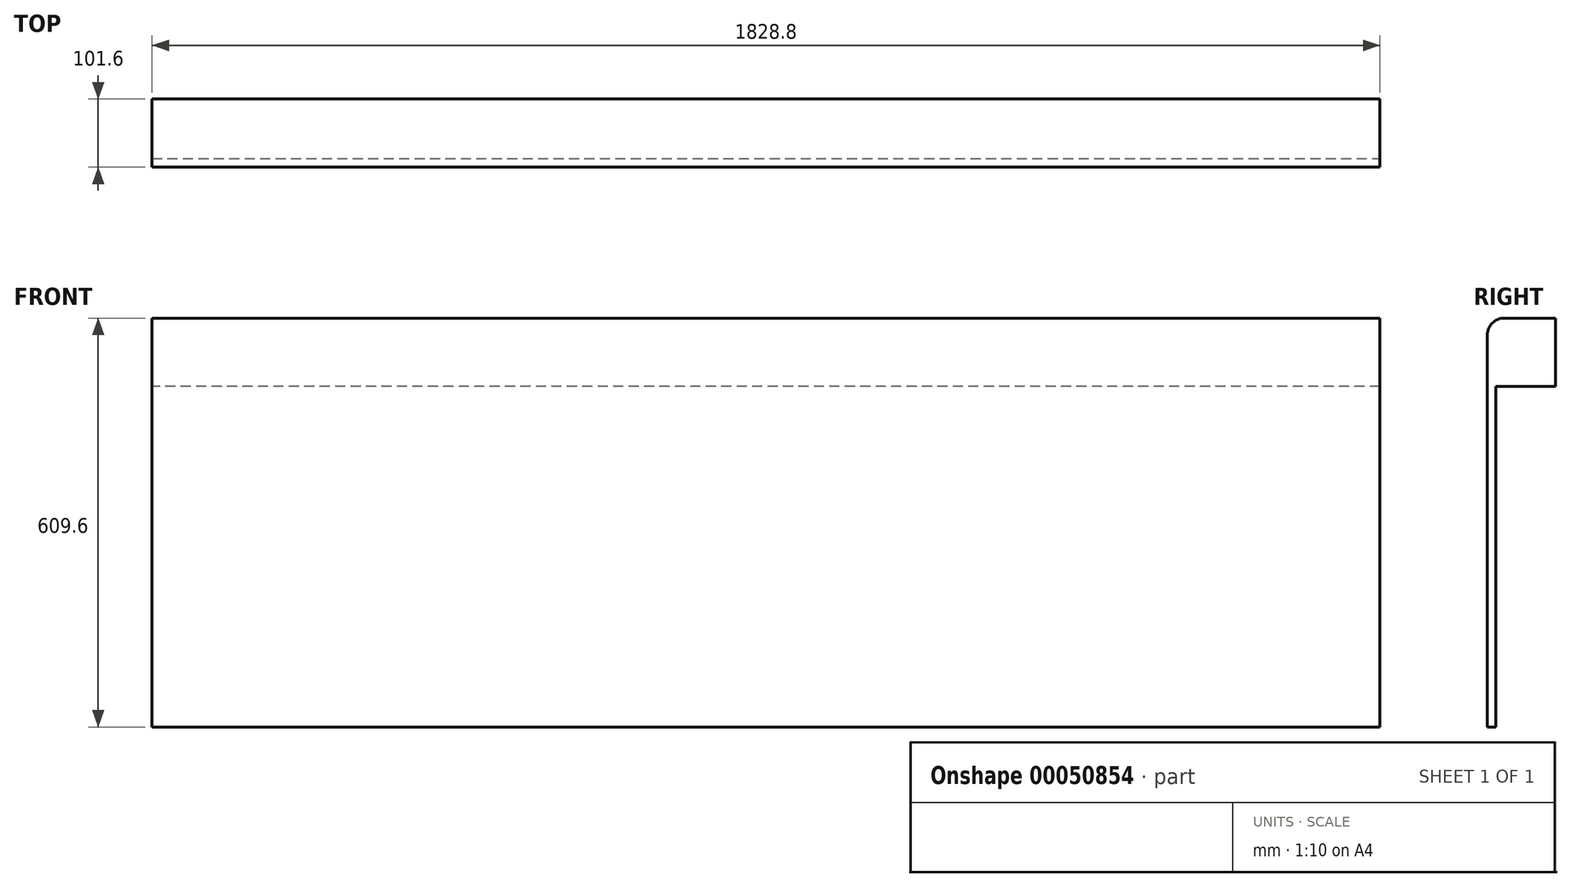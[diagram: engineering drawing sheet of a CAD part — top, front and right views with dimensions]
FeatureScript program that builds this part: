
annotation { "Feature Type Name" : "Feature", "Feature Type Description" : "" }
export const myFeature = defineFeature(function(context is Context, id is Id, definition is map)
    precondition{}
    {
        {
            var Q0;
            Q0=qCreatedBy(makeId("Front.planeOp"),FACE);
            var sketch = newSketch(context, id + "F0", { "sketchPlane" : qUnion([Q0])});
            skLineSegment(sketch, "E0.bottom", {"start": v(-914.4, 0) * mm, "end": v(914.4, 0) * mm});
            skLineSegment(sketch, "E0.top", {"start": v(-914.4, -609.6) * mm, "end": v(914.4, -609.6) * mm});
            skLineSegment(sketch, "E0.left", {"start": v(-914.4, 0) * mm, "end": v(-914.4, -609.6) * mm});
            skLineSegment(sketch, "E0.right", {"start": v(914.4, 0) * mm, "end": v(914.4, -609.6) * mm});
            skSolve(sketch);
        }
        {
            var Q0;
            Q0 = qSketchRegion(id + "F0", true);
            extrude(context, id + "F1", {"entities" : qUnion([Q0]), "depth" : 101.6 * mm});
        }
        {
            var Q0;
            Q0=makeQuery(id+"F1.opExtrude","CAP_FACE",FACE,{"disambiguationData":[OSD([sQuery(id+"F0.wireOp",EDGE,"E0.bottom"),sQuery(id+"F0.wireOp",EDGE,"E0.top"),sQuery(id+"F0.wireOp",EDGE,"E0.left"),sQuery(id+"F0.wireOp",EDGE,"E0.right")])],"isStart":true});
            var sketch = newSketch(context, id + "F2", { "sketchPlane" : qUnion([Q0])});
            skLineSegment(sketch, "E1.bottom", {"start": v(-914.4, -609.6) * mm, "end": v(914.4, -609.6) * mm});
            skLineSegment(sketch, "E1.top", {"start": v(-914.4, -101.6) * mm, "end": v(914.4, -101.6) * mm});
            skLineSegment(sketch, "E1.left", {"start": v(-914.4, -609.6) * mm, "end": v(-914.4, -101.6) * mm});
            skLineSegment(sketch, "E1.right", {"start": v(914.4, -609.6) * mm, "end": v(914.4, -101.6) * mm});
            skSolve(sketch);
        }
        {
            var Q0;
            Q0 = qSketchRegion(id + "F2", true);
            extrude(context, id + "F3", {"entities" : qUnion([Q0]), "operationType" : NewBodyOperationType.REMOVE, "oppositeDirection" : true, "depth" : 88.9 * mm});
        }
        {
            var Q0;
            Q0=makeQuery(id+"F1.opExtrude","CAP_EDGE",EDGE,{"disambiguationData":[OSD([sQuery(id+"F0.wireOp",EDGE,"E0.bottom")])],"isStart":false});
            fillet(context, id + "F4", {"entities" : qUnion([Q0]), "radius" : 25.4 * mm, "tangentPropagation" : true, "allowEdgeOverflow" : false});
        }
    });
